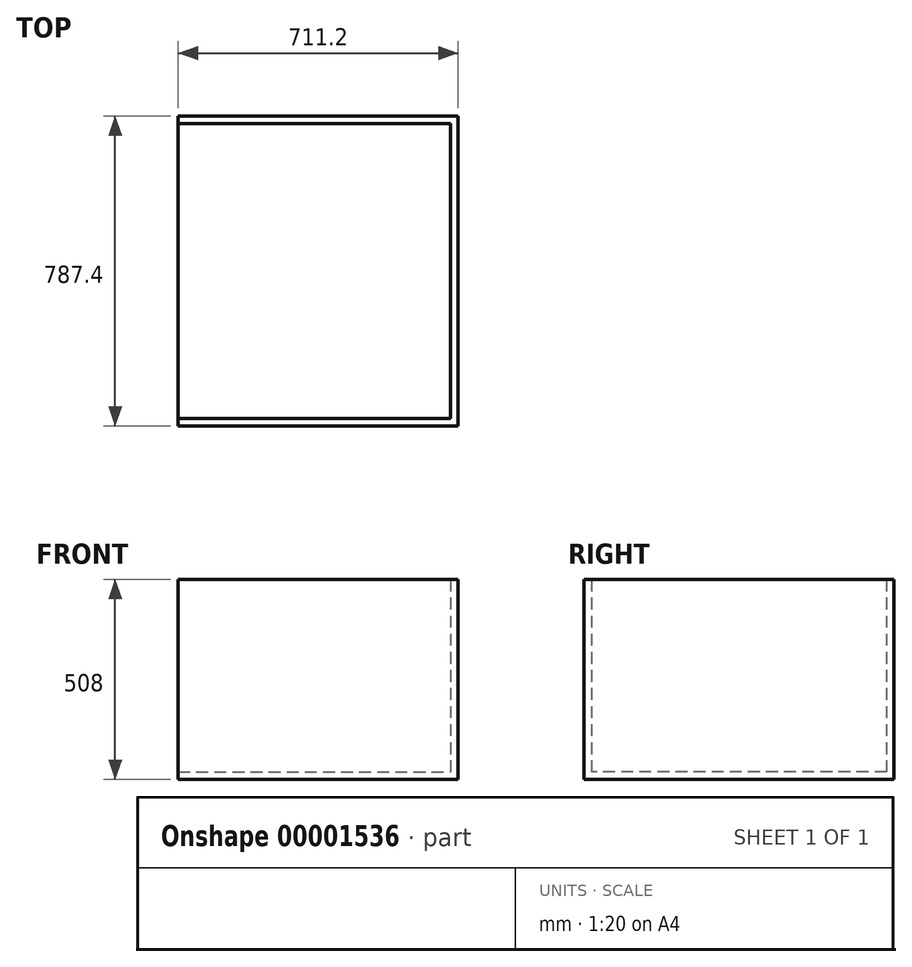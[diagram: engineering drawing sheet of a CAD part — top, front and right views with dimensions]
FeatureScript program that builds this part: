
annotation { "Feature Type Name" : "Feature", "Feature Type Description" : "" }
export const myFeature = defineFeature(function(context is Context, id is Id, definition is map)
    precondition{}
    {
        {
            var Q0;
            Q0=qCreatedBy(makeId("Top.planeOp"),FACE);
            var sketch = newSketch(context, id + "F0", { "sketchPlane" : qUnion([Q0])});
            skLineSegment(sketch, "E0.bottom", {"start": v(-355.6, 393.7) * mm, "end": v(355.6, 393.7) * mm});
            skLineSegment(sketch, "E0.top", {"start": v(-355.6, -393.7) * mm, "end": v(355.6, -393.7) * mm});
            skLineSegment(sketch, "E0.left", {"start": v(-355.6, 393.7) * mm, "end": v(-355.6, -393.7) * mm});
            skLineSegment(sketch, "E0.right", {"start": v(355.6, 393.7) * mm, "end": v(355.6, -393.7) * mm});
            skSolve(sketch);
        }
        {
            var Q0;
            Q0=makeQuery(id+"F0.imprint","IMPRINT",FACE,{"disambiguationData":[TD([[makeQuery(id+"F0.imprint","IMPRINT",EDGE,{"derivedFrom":sQuery(id+"F0.wireOp",EDGE,"E0.bottom")}),-1.0]])]});
            extrude(context, id + "F1", {"entities" : qUnion([Q0]), "depth" : 508 * mm});
        }
        {
            var Q0;
            Q0=makeQuery(id+"F1.opExtrude","CAP_FACE",FACE,{"disambiguationData":[OSD([sQuery(id+"F0.wireOp",EDGE,"E0.bottom"),sQuery(id+"F0.wireOp",EDGE,"E0.top"),sQuery(id+"F0.wireOp",EDGE,"E0.left"),sQuery(id+"F0.wireOp",EDGE,"E0.right")])],"isStart":false});
            var Q1;
            Q1=makeQuery(id+"F1.opExtrude","SWEPT_FACE",FACE,{"disambiguationData":[OSD([sQuery(id+"F0.wireOp",EDGE,"E0.left")])]});
            shell(context, id + "F2", {"entities" : qUnion([Q0, Q1]), "thickness" : 19.05 * mm});
        }
    });
